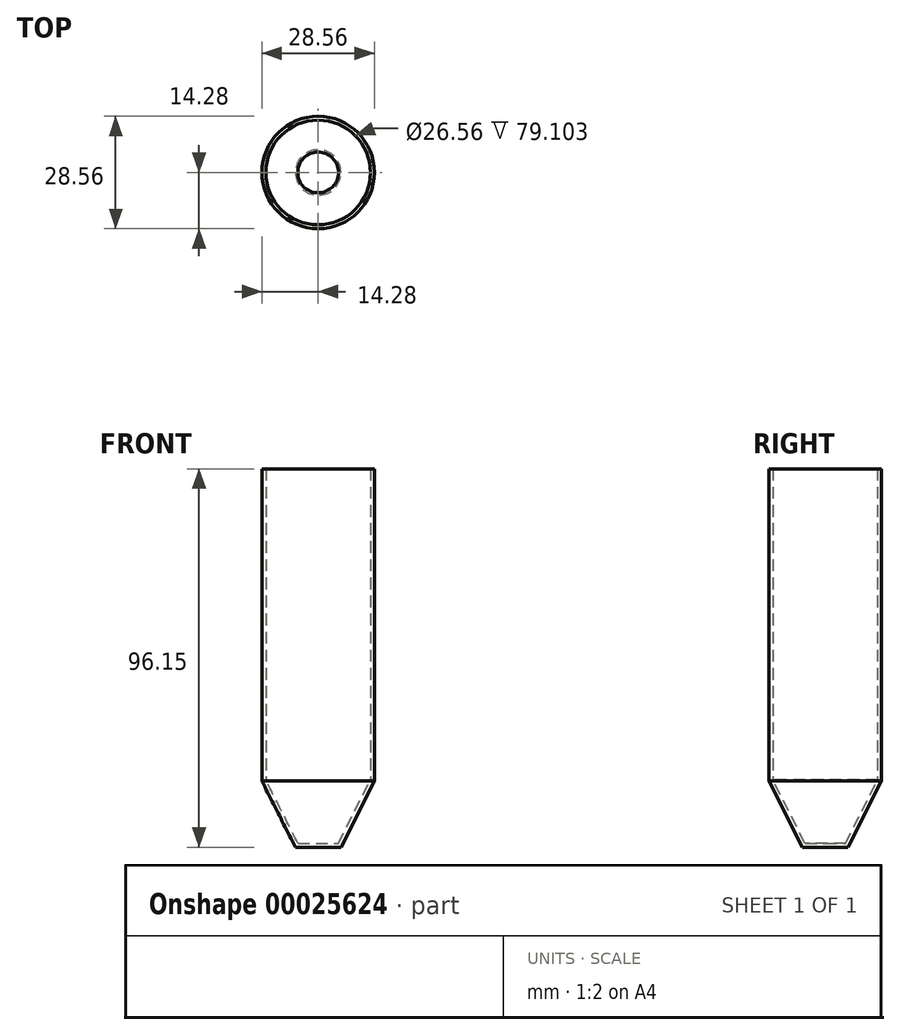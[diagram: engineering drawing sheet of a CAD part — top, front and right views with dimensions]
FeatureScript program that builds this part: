
annotation { "Feature Type Name" : "Feature", "Feature Type Description" : "" }
export const myFeature = defineFeature(function(context is Context, id is Id, definition is map)
    precondition{}
    {
        {
            var Q0;
            Q0=qCreatedBy(makeId("Front.planeOp"),FACE);
            var sketch = newSketch(context, id + "F0", { "sketchPlane" : qUnion([Q0])});
            skLineSegment(sketch, "E0", {"start": v(0, -16.8) * mm, "end": v(5.77, -16.8) * mm});
            skLineSegment(sketch, "E1", {"start": v(5.77, -16.8) * mm, "end": v(14.28, 0) * mm});
            skLineSegment(sketch, "E2", {"start": v(14.28, 0) * mm, "end": v(14.28, 79.34) * mm});
            skPoint(sketch, "E3.end.orphan", {"position": v(0, 98.18) * mm});
            skLineSegment(sketch, "E4.0", {"start": v(13.28, 0.24) * mm, "end": v(13.28, 79.34) * mm});
            skLineSegment(sketch, "E4.1", {"start": v(5.16, -15.8) * mm, "end": v(13.28, 0.24) * mm});
            skLineSegment(sketch, "E4.2", {"start": v(0, -15.8) * mm, "end": v(5.16, -15.8) * mm});
            skLineSegment(sketch, "E5", {"start": v(13.28, 79.34) * mm, "end": v(14.28, 79.34) * mm});
            skLineSegment(sketch, "E6", {"start": v(0, -16.8) * mm, "end": v(0, -15.8) * mm});
            skSolve(sketch);
        }
        {
            var Q0;
            Q0=makeQuery(id+"F0.imprint","IMPRINT",FACE,{"disambiguationData":[TD([[makeQuery(id+"F0.imprint","IMPRINT",EDGE,{"derivedFrom":sQuery(id+"F0.wireOp",EDGE,"E0")}),1.0]])]});
            var Q1;
            Q1=sQuery(id+"F0.wireOp",EDGE,"E6");
            revolve(context, id + "F1", {"entities" : qUnion([Q0]), "axis" : qUnion([Q1]), "revolveType" : RevolveType.FULL});
        }
    });
